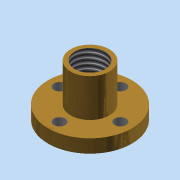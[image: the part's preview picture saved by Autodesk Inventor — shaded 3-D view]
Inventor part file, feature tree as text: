
AUTODESK INVENTOR PART (.ipt)
format: ipt  version: 2015 (Build 190159000, 159)  size: 113,664 bytes
history: native  units: mm
features: sketch x4, extrude x3, hole x1, pattern_circular x1, thread x1
ambient origin geometry x8: Origin, YZ Plane, XZ Plane, XY Plane, X Axis, Y Axis, Z Axis, Center Point
bodies: Solid1 (feature_tree)
feature tree (10):
  extrude  "Extrusion1"  Depth=3.5mm TaperAngle=0.0deg
  extrude  "Extrusion2"  Depth=10.0mm TaperAngle=0.0deg
  hole  "Hole1"  [1 undecoded]
  pattern_circular  "Circular Pattern1"  [2 undecoded]
  extrude  "Extrusion3"  Depth=10.0mm TaperAngle=0.0deg
  thread  "Thread1"  [1 undecoded]
  sketch  "Sketch1"  dims[d0=22.0mm d1=3.5mm d2=0.0mm]
  sketch  "Sketch2"  dims[d3=10.2mm d4=10.0mm d5=0.0mm]
  sketch  "Sketch3"  dims[d7=8.0mm]
  sketch  "Sketch4"  dims[d8=3.0mm d9=6.0mm d10=4.0mm d11=2.0mm d12=90.0deg d13=8.0mm d14=20.594885mm d15=40.0mm d16=360.0deg d18=8.0mm d19=10.0mm d20=0.0mm d21=10.0mm d22=0.0mm]
note: 4 required parameter values undecoded (feature->parameter linkage not recoverable at this tier; creation-order binding heuristic only, values carry confidence <= 0.55)
